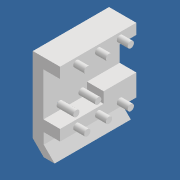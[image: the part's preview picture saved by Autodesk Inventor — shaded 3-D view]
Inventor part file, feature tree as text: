
AUTODESK INVENTOR PART (.ipt)
format: ipt  version: 2020 (Build 240168000, 168)  size: 189,952 bytes
history: native  units: mm
features: sketch x8, extrude x7, chamfer x2, split x1
ambient origin geometry x8: Origin, YZ Plane, XZ Plane, XY Plane, X Axis, Y Axis, Z Axis, Center Point
bodies: Solid1 (feature_tree)
feature tree (18):
  extrude  "Extrusion1"  Depth=56.0mm
  extrude  "Extrusion2"  Depth=40.0mm
  extrude  "Extrusion3"  Depth=7.8mm
  extrude  "Extrusion4"  Depth=4.6mm
  sketch  "Sketch14"  dims[d10=4.6mm d11=16.0mm]
  extrude  "Extrusion7"  Depth=16.0mm
  extrude  "Extrusion8"  Depth=12.0mm TaperAngle=0.0deg
  chamfer  "Chamfer1"  Distance=26.0mm
  chamfer  "Chamfer2"  Distance=24.0mm
  split  "Split1"
  extrude  "Extrusion9"  Depth=24.0mm
  sketch  "Sketch1"  dims[d0=39.6mm d1=56.0mm]
  sketch  "Sketch2"  dims[d2=40.0mm d3=0.0mm d4=24.4mm]
  sketch  "Sketch3"  dims[d5=31.8mm d6=7.8mm]
  sketch  "Sketch4"  dims[d7=64.0mm d8=0.0mm d9=4.6mm]
  sketch  "Sketch15"  dims[d12=12.0mm d13=26.0mm d14=0.0mm]
  sketch  "Sketch16"  dims[d15=24.0mm]
  sketch  "Sketch17"  dims[d16=8.0mm d17=26.0mm d18=0.0mm d35=24.0mm d36=0.0mm d37=24.0mm d38=8.0mm d39=8.0mm d40=8.0mm d41=8.0mm d42=8.0mm d43=16.0mm d44=0.0mm d45=0.0mm d46=8.0mm d47=2.0mm d48=45.0deg d49=8.0mm d50=2.0mm d51=45.0deg d52=4.6mm d53=4.6mm d54=4.6mm d55=4.6mm d56=4.6mm d57=4.6mm d58=12.0mm d59=16.0mm d60=16.0mm d61=4.0mm d62=40.0mm d63=8.0mm d64=0.0mm]
